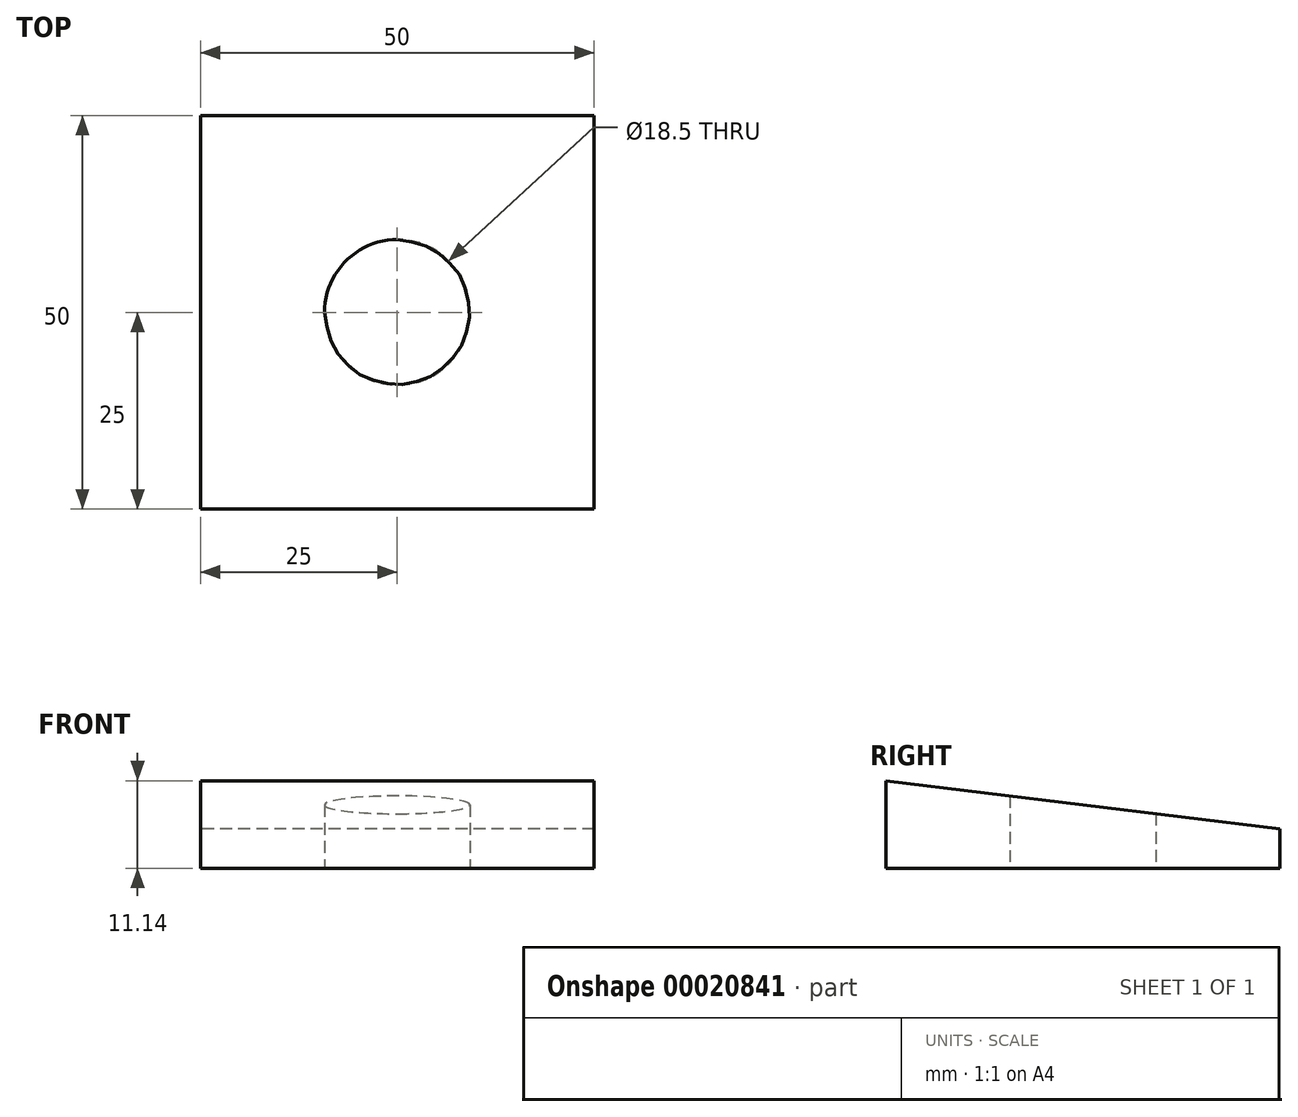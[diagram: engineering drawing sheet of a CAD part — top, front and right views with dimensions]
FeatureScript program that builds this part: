
annotation { "Feature Type Name" : "Feature", "Feature Type Description" : "" }
export const myFeature = defineFeature(function(context is Context, id is Id, definition is map)
    precondition{}
    {
        {
            var Q0;
            Q0=qCreatedBy(makeId("Right.planeOp"),FACE);
            var sketch = newSketch(context, id + "F0", { "sketchPlane" : qUnion([Q0])});
            skLineSegment(sketch, "E0", {"start": v(0, 0) * mm, "end": v(50, 0) * mm});
            skLineSegment(sketch, "E1", {"start": v(50, 0) * mm, "end": v(50, 5) * mm});
            skLineSegment(sketch, "E2", {"start": v(50, 5) * mm, "end": v(0, 11.14) * mm});
            skLineSegment(sketch, "E3", {"start": v(0, 11.14) * mm, "end": v(0, 0) * mm});
            skSolve(sketch);
        }
        {
            var Q0;
            Q0=makeQuery(id+"F0.imprint","IMPRINT",FACE,{"disambiguationData":[TD([[makeQuery(id+"F0.imprint","IMPRINT",EDGE,{"derivedFrom":sQuery(id+"F0.wireOp",EDGE,"E0")}),1.0]])]});
            extrude(context, id + "F1", {"entities" : qUnion([Q0]), "endBound" : BoundingType.SYMMETRIC, "depth" : 50 * mm});
        }
        {
            var Q0;
            Q0=qCreatedBy(makeId("Top.planeOp"),FACE);
            var sketch = newSketch(context, id + "F2", { "sketchPlane" : qUnion([Q0])});
            skPoint(sketch, "E4", {"position": v(0, 25) * mm});
            skSolve(sketch);
        }
        {
            var Q0;
            Q0=sQuery(id+"F2.wireOp",VERTEX,"E4");
            var Q1;
            Q1=makeQuery(id+"F1.opExtrude","SWEPT_BODY",BODY,{"disambiguationData":[OSD([sQuery(id+"F0.wireOp",EDGE,"E0"),sQuery(id+"F0.wireOp",EDGE,"E1"),sQuery(id+"F0.wireOp",EDGE,"E2"),sQuery(id+"F0.wireOp",EDGE,"E3")])]});
            hole(context, id + "F3", {"style" : HoleStyle.SIMPLE, "holeDiameter" : 18.5 * mm, "endStyle" : HoleEndStyle.THROUGH, "oppositeDirection" : true, "locations" : qUnion([Q0]), "scope" : qUnion([Q1])});
        }
    });
